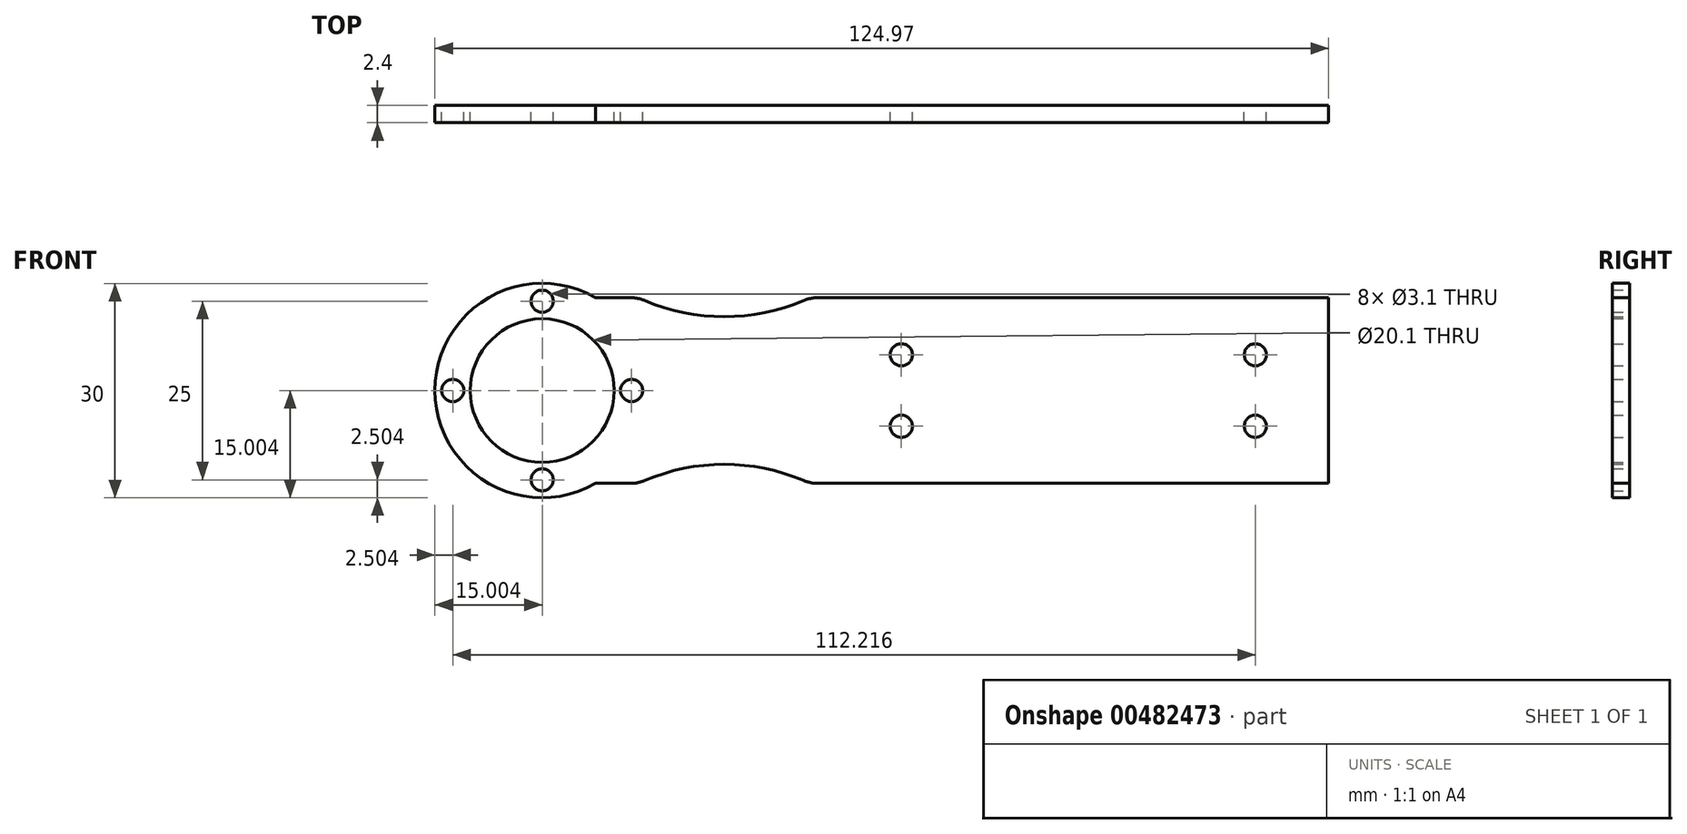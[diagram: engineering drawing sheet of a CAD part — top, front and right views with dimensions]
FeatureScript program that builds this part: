
annotation { "Feature Type Name" : "Feature", "Feature Type Description" : "" }
export const myFeature = defineFeature(function(context is Context, id is Id, definition is map)
    precondition{}
    {
        {
            var Q0;
            Q0=qCreatedBy(makeId("Front.planeOp"),FACE);
            var sketch = newSketch(context, id + "F0", { "sketchPlane" : qUnion([Q0])});
            skCircle(sketch, "E0", {"center": v(-96.85, 46.92) * mm, "radius": 1.55 * mm});
            skCircle(sketch, "E1", {"center": v(-96.85, 36.92) * mm, "radius": 1.55 * mm});
            skCircle(sketch, "E2", {"center": v(-47.35, 46.92) * mm, "radius": 1.55 * mm});
            skCircle(sketch, "E3", {"center": v(-47.35, 36.92) * mm, "radius": 1.55 * mm});
            skLineSegment(sketch, "E4", {"start": v(-37.1, 54.92) * mm, "end": v(-37.1, 28.92) * mm});
            skLineSegment(sketch, "E5", {"start": v(-107.1, 54.92) * mm, "end": v(-107.1, 28.92) * mm});
            skLineSegment(sketch, "E6", {"start": v(-37.1, 54.92) * mm, "end": v(-108.53, 54.92) * mm});
            skLineSegment(sketch, "E7", {"start": v(-37.1, 28.92) * mm, "end": v(-108.53, 28.92) * mm});
            skCircle(sketch, "E8", {"center": v(-147.07, 41.92) * mm, "radius": 10.05 * mm});
            skArc(sketch, "E9", {"start": v(-139.58, 54.92) * mm, "mid": v(-162.07, 41.92) * mm, "end": v(-139.58, 28.92) * mm});
            skPoint(sketch, "E10.trimOffspring.end.orphan", {"position": v(-93.1, 31.42) * mm});
            skPoint(sketch, "E11.left.start.orphan", {"position": v(-93.1, 52.42) * mm});
            skLineSegment(sketch, "E12", {"start": v(-147.07, 58.37) * mm, "end": v(-147.07, 25.7) * mm, "construction": true});
            skLineSegment(sketch, "E13", {"start": v(-166.39, 41.92) * mm, "end": v(-130.6, 41.92) * mm, "construction": true});
            skCircle(sketch, "E14", {"center": v(-147.07, 41.92) * mm, "radius": 12.5 * mm, "construction": true});
            skCircle(sketch, "E15", {"center": v(-147.07, 54.42) * mm, "radius": 1.55 * mm});
            skCircle(sketch, "E16", {"center": v(-159.57, 41.92) * mm, "radius": 1.55 * mm});
            skCircle(sketch, "E17", {"center": v(-134.57, 41.92) * mm, "radius": 1.55 * mm});
            skCircle(sketch, "E18", {"center": v(-147.07, 29.42) * mm, "radius": 1.55 * mm});
            skLineSegment(sketch, "E19", {"start": v(-163.95, 41.92) * mm, "end": v(-33.22, 41.92) * mm, "construction": true});
            skArc(sketch, "E20", {"start": v(-132.75, 54.53) * mm, "mid": v(-121.62, 52.26) * mm, "end": v(-110.49, 54.53) * mm});
            skArc(sketch, "E21.filletArc", {"start": v(-108.53, 54.92) * mm, "mid": v(-109.53, 54.82) * mm, "end": v(-110.49, 54.53) * mm});
            skLineSegment(sketch, "E22", {"start": v(-139.58, 54.92) * mm, "end": v(-134.7, 54.92) * mm});
            skPoint(sketch, "E23.visualSharp", {"position": v(-133.65, 54.92) * mm});
            skArc(sketch, "E23.filletArc", {"start": v(-132.75, 54.53) * mm, "mid": v(-133.71, 54.82) * mm, "end": v(-134.7, 54.92) * mm});
            skArc(sketch, "E24.MirrorCS", {"start": v(-132.75, 29.32) * mm, "mid": v(-121.62, 31.59) * mm, "end": v(-110.49, 29.32) * mm});
            skArc(sketch, "E25.MirrorCS", {"start": v(-108.53, 28.92) * mm, "mid": v(-109.53, 29.02) * mm, "end": v(-110.49, 29.32) * mm});
            skArc(sketch, "E26.MirrorCS", {"start": v(-132.75, 29.32) * mm, "mid": v(-133.71, 29.02) * mm, "end": v(-134.7, 28.92) * mm});
            skLineSegment(sketch, "E27.trimOffspring", {"start": v(-134.7, 28.92) * mm, "end": v(-139.58, 28.92) * mm});
            skSolve(sketch);
        }
        {
            var Q0;
            Q0 = qSketchRegion(id + "F0", true);
            extrude(context, id + "F1", {"entities" : qUnion([Q0]), "depth" : 2.4 * mm, "offsetDistance" : 25 * mm});
        }
    });
